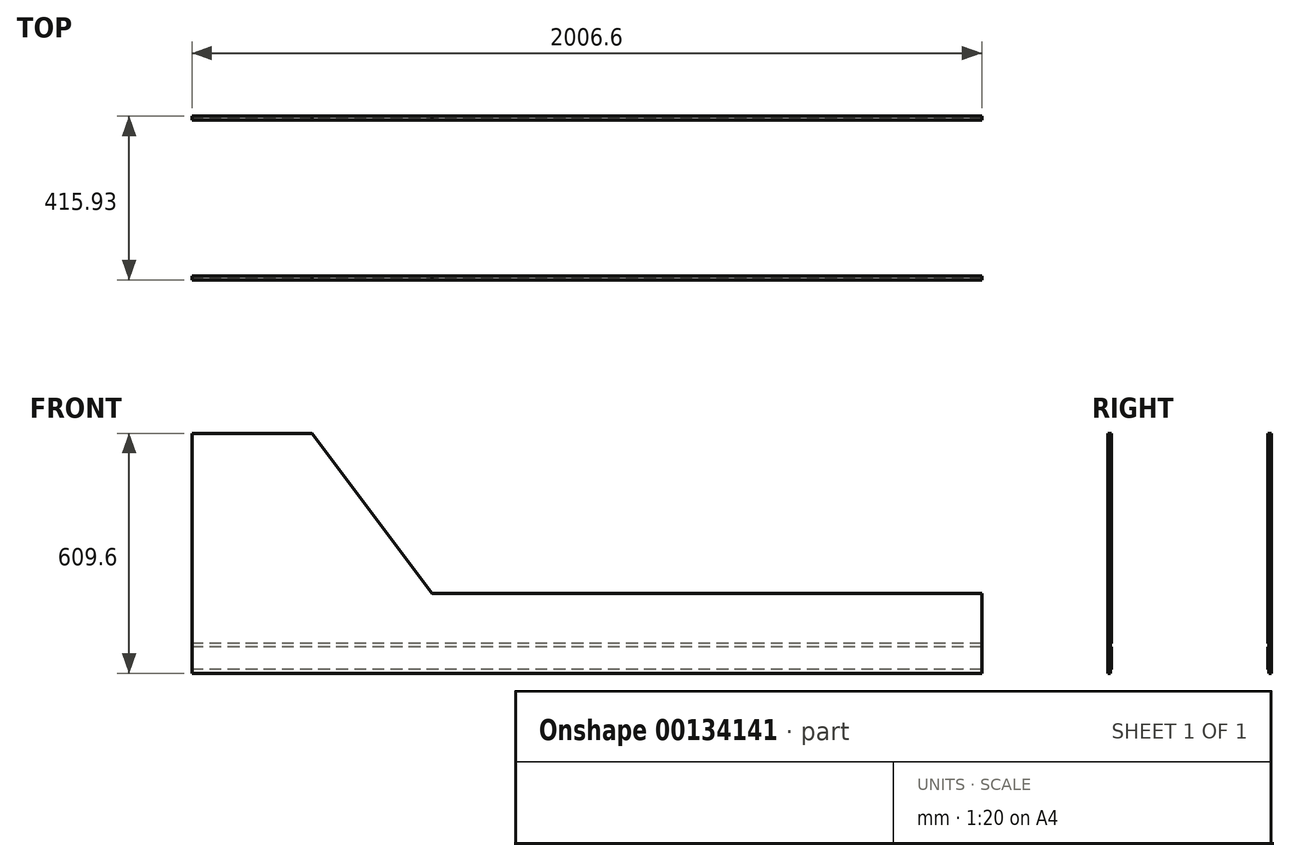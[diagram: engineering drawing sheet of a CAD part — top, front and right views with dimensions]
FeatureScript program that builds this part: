
annotation { "Feature Type Name" : "Feature", "Feature Type Description" : "" }
export const myFeature = defineFeature(function(context is Context, id is Id, definition is map)
    precondition{}
    {
        {
            var Q0;
            Q0=qCreatedBy(makeId("Front.planeOp"),FACE);
            var sketch = newSketch(context, id + "F0", { "sketchPlane" : qUnion([Q0])});
            skLineSegment(sketch, "E0", {"start": v(0, 0) * mm, "end": v(2006.6, 0) * mm});
            skLineSegment(sketch, "E1", {"start": v(2006.6, 0) * mm, "end": v(2006.6, 203.2) * mm});
            skLineSegment(sketch, "E2", {"start": v(2006.6, 203.2) * mm, "end": v(609.6, 203.2) * mm});
            skLineSegment(sketch, "E3", {"start": v(609.6, 203.2) * mm, "end": v(304.8, 609.6) * mm});
            skLineSegment(sketch, "E4", {"start": v(304.8, 609.6) * mm, "end": v(0, 609.6) * mm});
            skLineSegment(sketch, "E5", {"start": v(0, 609.6) * mm, "end": v(0, 0) * mm});
            skSolve(sketch);
        }
        {
            var Q0;
            Q0=makeQuery(id+"F0.imprint","IMPRINT",FACE,{"disambiguationData":[TD([[makeQuery(id+"F0.imprint","IMPRINT",EDGE,{"derivedFrom":sQuery(id+"F0.wireOp",EDGE,"E0")}),1.0]])]});
            extrude(context, id + "F1", {"entities" : qUnion([Q0]), "depth" : 9.52 * mm});
        }
        {
            var Q0;
            Q0=qCreatedBy(makeId("Right.planeOp"),FACE);
            var sketch = newSketch(context, id + "F2", { "sketchPlane" : qUnion([Q0])});
            skLineSegment(sketch, "E6.bottom", {"start": v(0, 0) * mm, "end": v(-3.18, 0) * mm});
            skLineSegment(sketch, "E6.top", {"start": v(0, 9.53) * mm, "end": v(-3.18, 9.53) * mm});
            skLineSegment(sketch, "E6.left", {"start": v(0, 0) * mm, "end": v(0, 9.53) * mm});
            skLineSegment(sketch, "E6.right", {"start": v(-3.18, 0) * mm, "end": v(-3.18, 9.53) * mm});
            skSolve(sketch);
        }
        {
            var Q0;
            Q0=qCreatedBy(makeId("Right.planeOp"),FACE);
            var sketch = newSketch(context, id + "F3", { "sketchPlane" : qUnion([Q0])});
            skLineSegment(sketch, "E7.bottom", {"start": v(0, 66.67) * mm, "end": v(-3.18, 66.67) * mm});
            skLineSegment(sketch, "E7.top", {"start": v(0, 76.2) * mm, "end": v(-3.18, 76.2) * mm});
            skLineSegment(sketch, "E7.left", {"start": v(0, 66.67) * mm, "end": v(0, 76.2) * mm});
            skLineSegment(sketch, "E7.right", {"start": v(-3.18, 66.67) * mm, "end": v(-3.18, 76.2) * mm});
            skSolve(sketch);
        }
        {
            var Q0;
            Q0=makeQuery(id+"F1.opExtrude","SWEPT_BODY",BODY,{"disambiguationData":[OSD([sQuery(id+"F0.wireOp",EDGE,"E0"),sQuery(id+"F0.wireOp",EDGE,"E1"),sQuery(id+"F0.wireOp",EDGE,"E2"),sQuery(id+"F0.wireOp",EDGE,"E3"),sQuery(id+"F0.wireOp",EDGE,"E4"),sQuery(id+"F0.wireOp",EDGE,"E5")])]});
            transform(context, id + "F4", {"entities" : qUnion([Q0]), "transformType" : TransformType.TRANSLATION_3D, "dx" : 0 * mm, "dy" : 628.16 * mm, "dz" : 0 * mm, "makeCopy" : true});
        }
        {
            var Q0;
            Q0=makeQuery(id+"F4.opPattern","COPY",BODY,{"derivedFrom":makeQuery(id+"F1.opExtrude","SWEPT_BODY",BODY,{"disambiguationData":[OSD([sQuery(id+"F0.wireOp",EDGE,"E0"),sQuery(id+"F0.wireOp",EDGE,"E1"),sQuery(id+"F0.wireOp",EDGE,"E2"),sQuery(id+"F0.wireOp",EDGE,"E3"),sQuery(id+"F0.wireOp",EDGE,"E4"),sQuery(id+"F0.wireOp",EDGE,"E5")])]}),"instanceName":"1"});
            deleteBodies(context, id + "F5", {"entities" : qUnion([Q0])});
        }
        {
            var Q0;
            Q0=makeQuery(id+"F1.opExtrude","SWEPT_BODY",BODY,{"disambiguationData":[OSD([sQuery(id+"F0.wireOp",EDGE,"E0"),sQuery(id+"F0.wireOp",EDGE,"E1"),sQuery(id+"F0.wireOp",EDGE,"E2"),sQuery(id+"F0.wireOp",EDGE,"E3"),sQuery(id+"F0.wireOp",EDGE,"E4"),sQuery(id+"F0.wireOp",EDGE,"E5")])]});
            transform(context, id + "F6", {"entities" : qUnion([Q0]), "transformType" : TransformType.TRANSLATION_3D, "dx" : 0 * mm, "dy" : 406.4 * mm, "dz" : 0 * mm, "makeCopy" : true});
        }
        {
            var Q0;
            Q0 = qSketchRegion(id + "F2", true);
            extrude(context, id + "F7", {"entities" : qUnion([Q0]), "operationType" : NewBodyOperationType.REMOVE, "endBound" : BoundingType.THROUGH_ALL, "depth" : 25.4 * mm});
        }
        {
            var Q0;
            Q0 = qSketchRegion(id + "F3", true);
            extrude(context, id + "F8", {"entities" : qUnion([Q0]), "operationType" : NewBodyOperationType.REMOVE, "endBound" : BoundingType.THROUGH_ALL, "depth" : 25.4 * mm});
        }
        {
            var Q0;
            Q0=qCreatedBy(makeId("Right.planeOp"),FACE);
            var sketch = newSketch(context, id + "F9", { "sketchPlane" : qUnion([Q0])});
            skLineSegment(sketch, "E8.bottom", {"start": v(396.88, 0) * mm, "end": v(400.05, 0) * mm});
            skLineSegment(sketch, "E8.top", {"start": v(396.88, 9.53) * mm, "end": v(400.05, 9.53) * mm});
            skLineSegment(sketch, "E8.left", {"start": v(396.88, 0) * mm, "end": v(396.88, 9.53) * mm});
            skLineSegment(sketch, "E8.right", {"start": v(400.05, 0) * mm, "end": v(400.05, 9.53) * mm});
            skSolve(sketch);
        }
        {
            var Q0;
            Q0 = qSketchRegion(id + "F9", true);
            extrude(context, id + "F10", {"entities" : qUnion([Q0]), "operationType" : NewBodyOperationType.REMOVE, "endBound" : BoundingType.THROUGH_ALL, "depth" : 25.4 * mm});
        }
        {
            var Q0;
            Q0=qCreatedBy(makeId("Right.planeOp"),FACE);
            var sketch = newSketch(context, id + "F11", { "sketchPlane" : qUnion([Q0])});
            skLineSegment(sketch, "E9.bottom", {"start": v(396.88, 76.2) * mm, "end": v(400.05, 76.2) * mm});
            skLineSegment(sketch, "E9.top", {"start": v(396.88, 66.67) * mm, "end": v(400.05, 66.67) * mm});
            skLineSegment(sketch, "E9.left", {"start": v(396.88, 76.2) * mm, "end": v(396.88, 66.68) * mm});
            skLineSegment(sketch, "E9.right", {"start": v(400.05, 76.2) * mm, "end": v(400.05, 66.68) * mm});
            skSolve(sketch);
        }
        {
            var Q0;
            Q0 = qSketchRegion(id + "F11", true);
            extrude(context, id + "F12", {"entities" : qUnion([Q0]), "operationType" : NewBodyOperationType.REMOVE, "endBound" : BoundingType.THROUGH_ALL, "depth" : 25.4 * mm});
        }
    });
